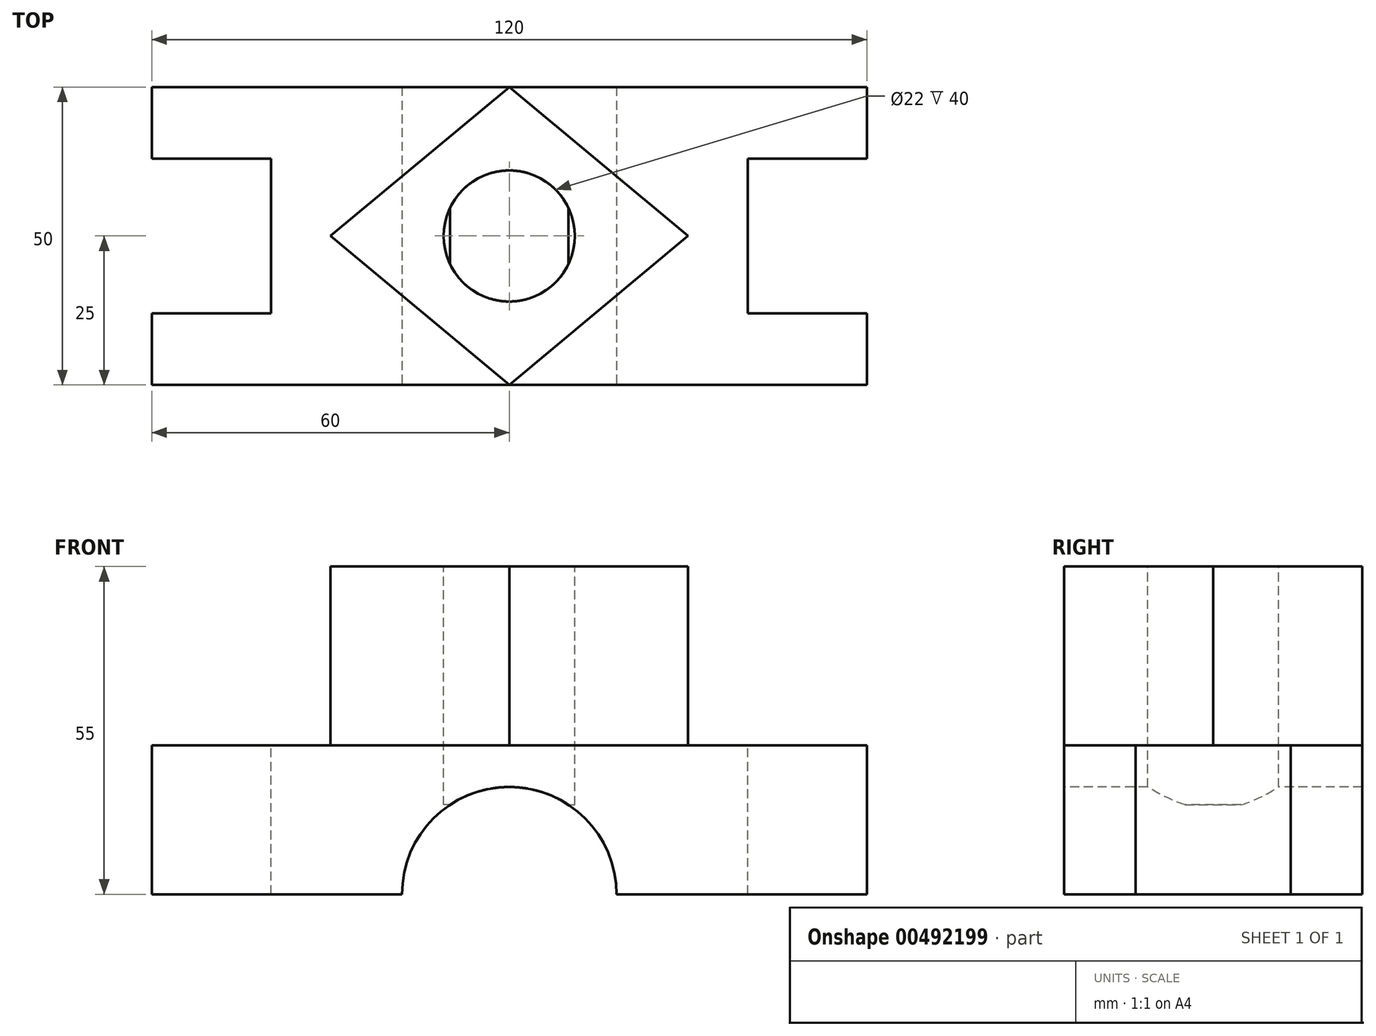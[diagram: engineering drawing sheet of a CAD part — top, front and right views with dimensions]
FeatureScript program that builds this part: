
annotation { "Feature Type Name" : "Feature", "Feature Type Description" : "" }
export const myFeature = defineFeature(function(context is Context, id is Id, definition is map)
    precondition{}
    {
        {
            var Q0;
            Q0=qCreatedBy(makeId("Front.planeOp"),FACE);
            var sketch = newSketch(context, id + "F0", { "sketchPlane" : qUnion([Q0])});
            skLineSegment(sketch, "E0.bottom", {"start": v(-60, -12.5) * mm, "end": v(60, -12.5) * mm});
            skLineSegment(sketch, "E0.top", {"start": v(-60, 12.5) * mm, "end": v(-30, 12.5) * mm});
            skLineSegment(sketch, "E0.left", {"start": v(-60, -12.5) * mm, "end": v(-60, 12.5) * mm});
            skLineSegment(sketch, "E0.right", {"start": v(60, -12.5) * mm, "end": v(60, 12.5) * mm});
            skPoint(sketch, "E0.middle", {"position": v(0, 0) * mm});
            skPoint(sketch, "E1.middle", {"position": v(0, 12.5) * mm});
            skPoint(sketch, "E2.orphan", {"position": v(-30, -5.54) * mm});
            skPoint(sketch, "E3.orphan", {"position": v(30, -5.54) * mm});
            skLineSegment(sketch, "E4.trimOffspring", {"start": v(30, 12.5) * mm, "end": v(60, 12.5) * mm});
            skLineSegment(sketch, "E5", {"start": v(-30, 12.5) * mm, "end": v(30, 12.5) * mm});
            skSolve(sketch);
        }
        {
            var Q0;
            Q0 = qSketchRegion(id + "F0", true);
            extrude(context, id + "F1", {"entities" : qUnion([Q0]), "depth" : 50 * mm});
        }
        {
            var Q0;
            Q0=makeQuery(id+"F1.opExtrude","CAP_FACE",FACE,{"disambiguationData":[OSD([sQuery(id+"F0.wireOp",EDGE,"E0.bottom"),sQuery(id+"F0.wireOp",EDGE,"E0.top"),sQuery(id+"F0.wireOp",EDGE,"E0.left"),sQuery(id+"F0.wireOp",EDGE,"E0.right"),sQuery(id+"F0.wireOp",EDGE,"E1.bottom"),sQuery(id+"F0.wireOp",EDGE,"E1.left"),sQuery(id+"F0.wireOp",EDGE,"E1.right"),sQuery(id+"F0.wireOp",EDGE,"E4.trimOffspring")])],"isStart":false});
            var sketch = newSketch(context, id + "F2", { "sketchPlane" : qUnion([Q0])});
            skPoint(sketch, "E6.center.orphan", {"position": v(0, -12.5) * mm});
            skCircle(sketch, "E7", {"center": v(0, -12.5) * mm, "radius": 18 * mm});
            skSolve(sketch);
        }
        {
            var Q0;
            Q0 = qSketchRegion(id + "F2", true);
            extrude(context, id + "F3", {"entities" : qUnion([Q0]), "operationType" : NewBodyOperationType.REMOVE, "oppositeDirection" : true, "depth" : 60 * mm});
        }
        {
            var Q0;
            Q0=makeQuery(id+"F1.opExtrude","SWEPT_FACE",FACE,{"disambiguationData":[OSD([sQuery(id+"F0.wireOp",EDGE,"E0.top"),sQuery(id+"F0.wireOp",EDGE,"E4.trimOffspring"),sQuery(id+"F0.wireOp",EDGE,"E5")])]});
            var sketch = newSketch(context, id + "F4", { "sketchPlane" : qUnion([Q0])});
            skLineSegment(sketch, "E8.bottom", {"start": v(-40, -38) * mm, "end": v(-80, -38) * mm});
            skLineSegment(sketch, "E8.top", {"start": v(-40, -12) * mm, "end": v(-80, -12) * mm});
            skLineSegment(sketch, "E8.left", {"start": v(-40, -38) * mm, "end": v(-40, -12) * mm});
            skLineSegment(sketch, "E8.right", {"start": v(-80, -38) * mm, "end": v(-80, -12) * mm});
            skPoint(sketch, "E8.middle", {"position": v(-60, -25) * mm});
            skLineSegment(sketch, "E9.bottom", {"start": v(40, -38) * mm, "end": v(80, -38) * mm});
            skLineSegment(sketch, "E9.top", {"start": v(40, -12) * mm, "end": v(80, -12) * mm});
            skLineSegment(sketch, "E9.left", {"start": v(40, -38) * mm, "end": v(40, -12) * mm});
            skLineSegment(sketch, "E9.right", {"start": v(80, -38) * mm, "end": v(80, -12) * mm});
            skPoint(sketch, "E9.middle", {"position": v(60, -25) * mm});
            skSolve(sketch);
        }
        {
            var Q0;
            Q0 = qSketchRegion(id + "F4", true);
            extrude(context, id + "F5", {"entities" : qUnion([Q0]), "operationType" : NewBodyOperationType.REMOVE, "oppositeDirection" : true, "depth" : 25 * mm});
        }
        {
            var Q0;
            Q0=makeQuery(id+"F1.opExtrude","SWEPT_FACE",FACE,{"disambiguationData":[OSD([sQuery(id+"F0.wireOp",EDGE,"E0.top"),sQuery(id+"F0.wireOp",EDGE,"E4.trimOffspring"),sQuery(id+"F0.wireOp",EDGE,"E5")])]});
            var sketch = newSketch(context, id + "F6", { "sketchPlane" : qUnion([Q0])});
            skPoint(sketch, "E10.middle", {"position": v(0, -25) * mm});
            skPoint(sketch, "E10.middle.positionSnap0", {"position": v(-40, -25) * mm});
            skPoint(sketch, "E10.centerSnap0", {"position": v(-40, -25) * mm});
            skLineSegment(sketch, "E11", {"start": v(0, 0) * mm, "end": v(-30, -25) * mm});
            skLineSegment(sketch, "E12", {"start": v(-30, -25) * mm, "end": v(0, -50) * mm});
            skLineSegment(sketch, "E13", {"start": v(0, -50) * mm, "end": v(30, -25) * mm});
            skLineSegment(sketch, "E14", {"start": v(30, -25) * mm, "end": v(0, 0) * mm});
            skPoint(sketch, "E15.orphan", {"position": v(30, 0) * mm});
            skPoint(sketch, "E10.top.start.orphan", {"position": v(-30, 0) * mm});
            skPoint(sketch, "E16.orphan", {"position": v(-30, -50) * mm});
            skPoint(sketch, "E10.bottom.end.orphan", {"position": v(30, -50) * mm});
            skSolve(sketch);
        }
        {
            var Q0;
            Q0 = qSketchRegion(id + "F6", true);
            var Q1;
            Q1 = qSketchRegion(id + "F8", true);
            extrude(context, id + "F7", {"entities" : qUnion([Q0, Q1]), "operationType" : NewBodyOperationType.ADD, "depth" : 30 * mm});
        }
        {
            var Q0;
            Q0=makeQuery(id+"F7.opExtrude","CAP_FACE",FACE,{"disambiguationData":[OSD([sQuery(id+"F6.wireOp",EDGE,"E11"),sQuery(id+"F6.wireOp",EDGE,"E12"),sQuery(id+"F6.wireOp",EDGE,"E13"),sQuery(id+"F6.wireOp",EDGE,"E14")])],"isStart":false});
            var sketch = newSketch(context, id + "F8", { "sketchPlane" : qUnion([Q0])});
            skCircle(sketch, "E17", {"center": v(0, -25) * mm, "radius": 11 * mm});
            skSolve(sketch);
        }
        {
            var Q0;
            Q0 = qSketchRegion(id + "F8", true);
            extrude(context, id + "F9", {"entities" : qUnion([Q0]), "operationType" : NewBodyOperationType.REMOVE, "oppositeDirection" : true, "depth" : 40 * mm});
        }
    });
